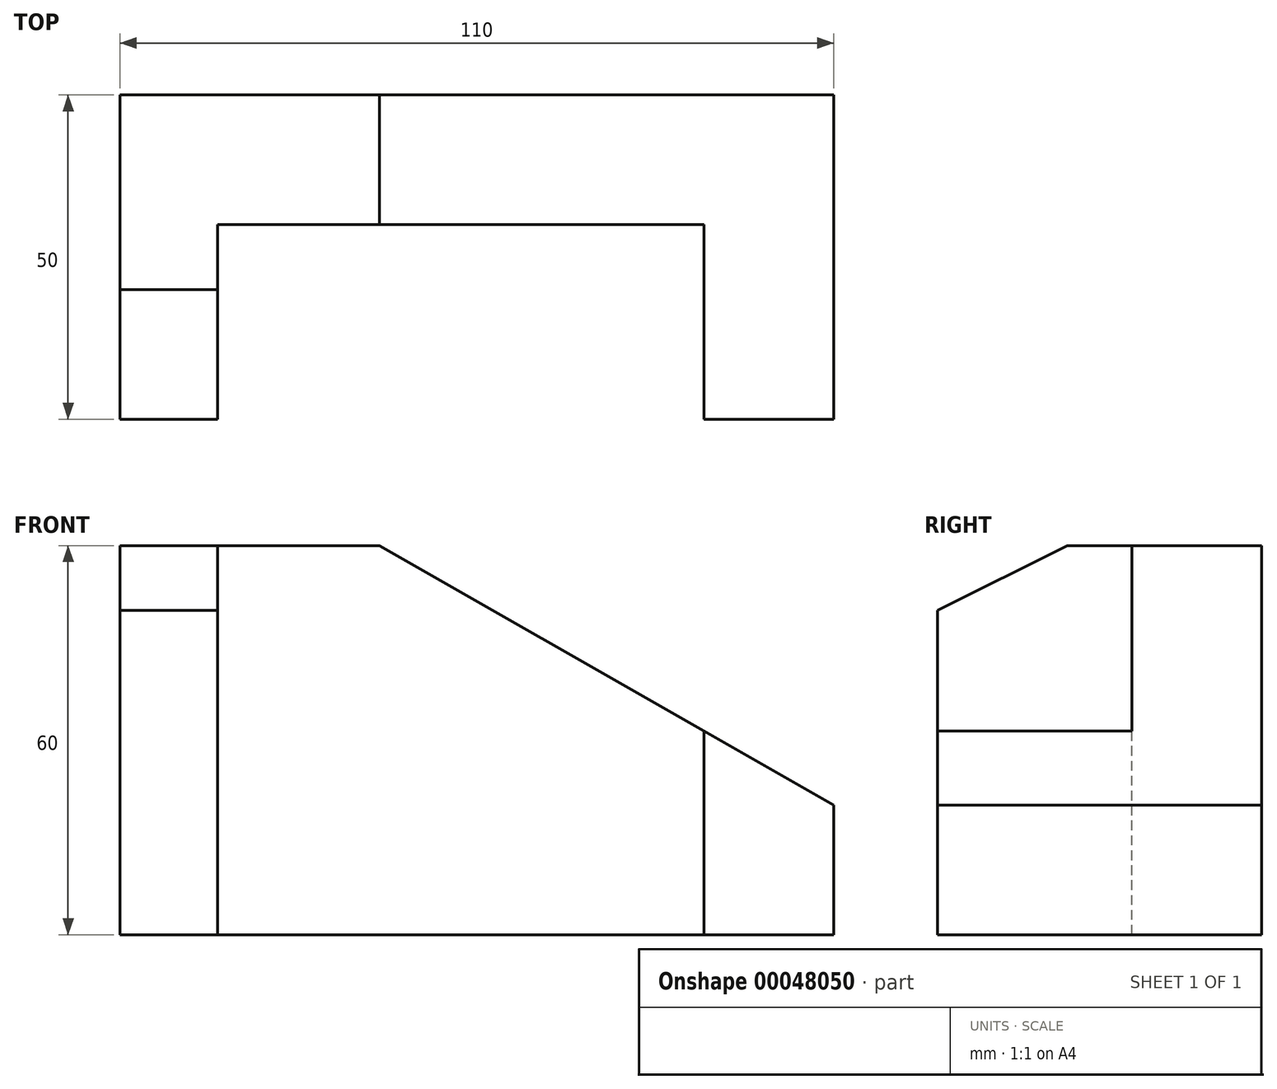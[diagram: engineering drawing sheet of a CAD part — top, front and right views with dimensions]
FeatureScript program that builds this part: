
annotation { "Feature Type Name" : "Feature", "Feature Type Description" : "" }
export const myFeature = defineFeature(function(context is Context, id is Id, definition is map)
    precondition{}
    {
        {
            var Q0;
            Q0=qCreatedBy(makeId("Front.planeOp"),FACE);
            var sketch = newSketch(context, id + "F0", { "sketchPlane" : qUnion([Q0])});
            skLineSegment(sketch, "E0", {"start": v(0, 0) * mm, "end": v(15, 0) * mm});
            skLineSegment(sketch, "E1", {"start": v(15, 0) * mm, "end": v(90, 0) * mm});
            skLineSegment(sketch, "E2", {"start": v(90, 0) * mm, "end": v(110, 0) * mm});
            skLineSegment(sketch, "E3", {"start": v(110, 0) * mm, "end": v(110, 20) * mm});
            skLineSegment(sketch, "E4", {"start": v(110, 20) * mm, "end": v(90, 31.43) * mm});
            skLineSegment(sketch, "E5", {"start": v(90, 31.43) * mm, "end": v(40, 60) * mm});
            skLineSegment(sketch, "E6", {"start": v(40, 60) * mm, "end": v(15, 60) * mm});
            skLineSegment(sketch, "E7", {"start": v(15, 60) * mm, "end": v(0, 60) * mm});
            skLineSegment(sketch, "E8", {"start": v(0, 60) * mm, "end": v(0, 0) * mm});
            skLineSegment(sketch, "E9", {"start": v(15, 0) * mm, "end": v(15, 60) * mm});
            skLineSegment(sketch, "E10", {"start": v(90, 31.43) * mm, "end": v(90, 0) * mm});
            skSolve(sketch);
        }
        {
            var Q0;
            Q0=makeQuery(id+"F0.imprint","IMPRINT",FACE,{"disambiguationData":[TD([[makeQuery(id+"F0.imprint","IMPRINT",EDGE,{"derivedFrom":sQuery(id+"F0.wireOp",EDGE,"E0")}),1.0]])]});
            extrude(context, id + "F1", {"entities" : qUnion([Q0]), "depth" : 50 * mm});
        }
        {
            var Q0;
            Q0=makeQuery(id+"F0.imprint","IMPRINT",FACE,{"disambiguationData":[TD([[makeQuery(id+"F0.imprint","IMPRINT",EDGE,{"derivedFrom":sQuery(id+"F0.wireOp",EDGE,"E1")}),1.0]])]});
            extrude(context, id + "F2", {"entities" : qUnion([Q0]), "operationType" : NewBodyOperationType.ADD, "depth" : 20 * mm});
        }
        {
            var Q0;
            Q0=makeQuery(id+"F0.imprint","IMPRINT",FACE,{"disambiguationData":[TD([[makeQuery(id+"F0.imprint","IMPRINT",EDGE,{"derivedFrom":sQuery(id+"F0.wireOp",EDGE,"E2")}),1.0]])]});
            extrude(context, id + "F3", {"entities" : qUnion([Q0]), "operationType" : NewBodyOperationType.ADD, "depth" : 50 * mm});
        }
        {
            var Q0;
            Q0=makeQuery(id+"F1.opExtrude","SWEPT_FACE",FACE,{"disambiguationData":[OSD([sQuery(id+"F0.wireOp",EDGE,"E9")])]});
            var sketch = newSketch(context, id + "F4", { "sketchPlane" : qUnion([Q0])});
            skLineSegment(sketch, "E11", {"start": v(-50, 50) * mm, "end": v(-30, 60) * mm});
            skLineSegment(sketch, "E12", {"start": v(-30, 60) * mm, "end": v(-50, 60) * mm});
            skLineSegment(sketch, "E13", {"start": v(-50, 60) * mm, "end": v(-50, 50) * mm});
            skSolve(sketch);
        }
        {
            var Q0;
            Q0=makeQuery(id+"F4.imprint","IMPRINT",FACE,{"disambiguationData":[TD([[makeQuery(id+"F4.imprint","IMPRINT",EDGE,{"derivedFrom":sQuery(id+"F4.wireOp",EDGE,"E11")}),1.0]])]});
            extrude(context, id + "F5", {"entities" : qUnion([Q0]), "operationType" : NewBodyOperationType.REMOVE, "endBound" : BoundingType.THROUGH_ALL, "oppositeDirection" : true, "depth" : 25 * mm});
        }
    });
